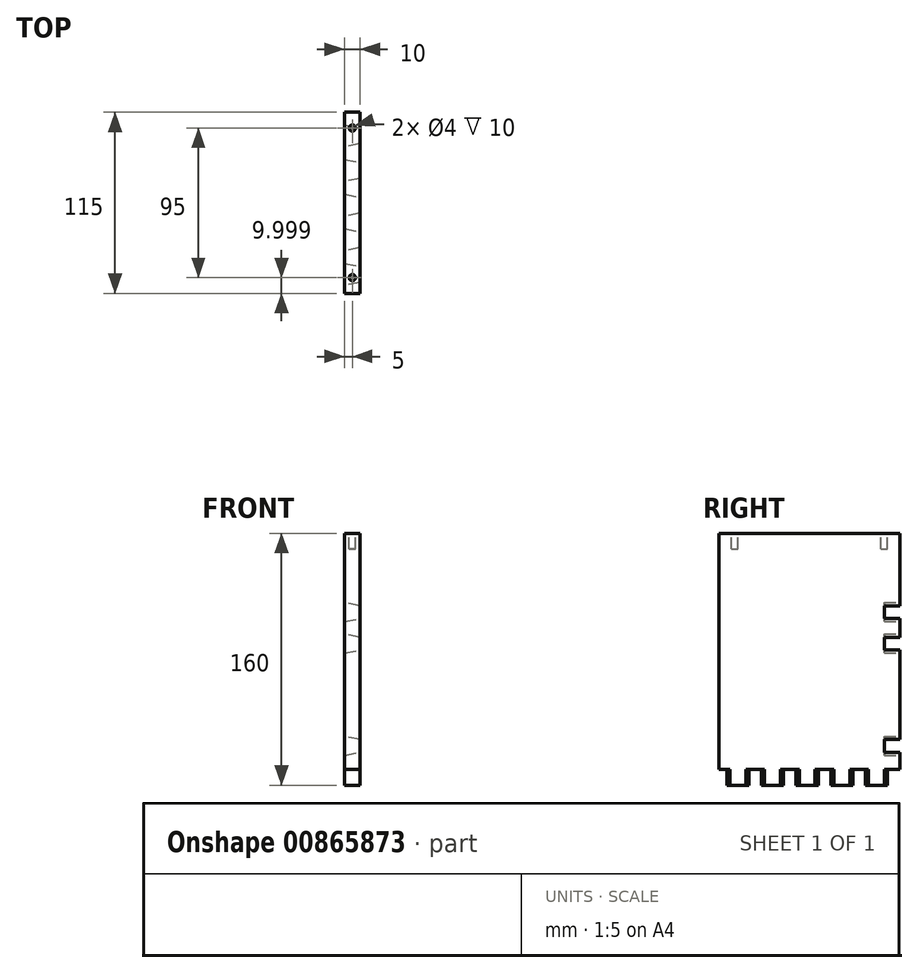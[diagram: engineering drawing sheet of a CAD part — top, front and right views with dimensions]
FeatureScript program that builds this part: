
annotation { "Feature Type Name" : "Feature", "Feature Type Description" : "" }
export const myFeature = defineFeature(function(context is Context, id is Id, definition is map)
    precondition{}
    {
        {
            var Q0;
            Q0=qCreatedBy(makeId("Right.planeOp"),FACE);
            var sketch = newSketch(context, id + "F0", { "sketchPlane" : qUnion([Q0])});
            skLineSegment(sketch, "E0.bottom", {"start": v(83.6, 91.6) * mm, "end": v(-31.4, 91.6) * mm});
            skLineSegment(sketch, "E0.left", {"start": v(83.6, 91.6) * mm, "end": v(83.6, -68.4) * mm});
            skLineSegment(sketch, "E0.right", {"start": v(-31.4, 91.6) * mm, "end": v(-31.4, -68.4) * mm});
            skLineSegment(sketch, "E1", {"start": v(83.6, -68.4) * mm, "end": v(-31.4, -68.4) * mm});
            skSolve(sketch);
        }
        {
            var Q0;
            Q0 = qSketchRegion(id + "F0", true);
            extrude(context, id + "F1", {"entities" : qUnion([Q0]), "depth" : 10 * mm, "offsetDistance" : 25 * mm});
        }
        {
            var Q0;
            Q0=makeQuery(id+"F1.opExtrude","SWEPT_FACE",FACE,{"disambiguationData":[OSD([sQuery(id+"F0.wireOp",EDGE,"E0.left")])]});
            var sketch = newSketch(context, id + "F2", { "sketchPlane" : qUnion([Q0])});
            skLineSegment(sketch, "E2", {"start": v(-10, 25.6) * mm, "end": v(0, 27.6) * mm});
            skLineSegment(sketch, "E3", {"start": v(0, 27.6) * mm, "end": v(0, 15.6) * mm});
            skLineSegment(sketch, "E4", {"start": v(0, 15.6) * mm, "end": v(-10, 17.6) * mm});
            skLineSegment(sketch, "E5", {"start": v(-10, 17.6) * mm, "end": v(-10, 25.6) * mm});
            skLineSegment(sketch, "E6", {"start": v(-10, 45.6) * mm, "end": v(0, 47.6) * mm});
            skLineSegment(sketch, "E7", {"start": v(0, 47.6) * mm, "end": v(0, 35.6) * mm});
            skLineSegment(sketch, "E8", {"start": v(0, 35.6) * mm, "end": v(-10, 37.6) * mm});
            skLineSegment(sketch, "E9", {"start": v(-10, 37.6) * mm, "end": v(-10, 45.6) * mm});
            skLineSegment(sketch, "E10", {"start": v(-10, -39.4) * mm, "end": v(0, -37.4) * mm});
            skLineSegment(sketch, "E11", {"start": v(0, -37.4) * mm, "end": v(0, -49.4) * mm});
            skLineSegment(sketch, "E12", {"start": v(0, -49.4) * mm, "end": v(-10, -47.4) * mm});
            skLineSegment(sketch, "E13", {"start": v(-10, -47.4) * mm, "end": v(-10, -39.4) * mm});
            skPoint(sketch, "E14", {"position": v(-10, 11.6) * mm});
            skSolve(sketch);
        }
        {
            var Q0;
            Q0 = qSketchRegion(id + "F2", true);
            extrude(context, id + "F3", {"entities" : qUnion([Q0]), "operationType" : NewBodyOperationType.REMOVE, "oppositeDirection" : true, "depth" : 10 * mm, "offsetDistance" : 25 * mm});
        }
        {
            var Q0;
            Q0=makeQuery(id+"F1.opExtrude","SWEPT_FACE",FACE,{"disambiguationData":[OSD([sQuery(id+"F0.wireOp",EDGE,"E1")])]});
            var sketch = newSketch(context, id + "F4", { "sketchPlane" : qUnion([Q0])});
            skLineSegment(sketch, "E15", {"start": v(10, -85.6) * mm, "end": v(0, -83.6) * mm});
            skLineSegment(sketch, "E16", {"start": v(0, -83.6) * mm, "end": v(0, -75.6) * mm});
            skLineSegment(sketch, "E17", {"start": v(0, -75.6) * mm, "end": v(10, -73.6) * mm});
            skLineSegment(sketch, "E18", {"start": v(10, -73.6) * mm, "end": v(10, -85.6) * mm});
            skLineSegment(sketch, "E19.0.1.0", {"start": v(0, -53.6) * mm, "end": v(10, -51.6) * mm});
            skLineSegment(sketch, "E19.0.1.1", {"start": v(10, -63.6) * mm, "end": v(0, -61.6) * mm});
            skLineSegment(sketch, "E19.0.1.2", {"start": v(10, -51.6) * mm, "end": v(10, -63.6) * mm});
            skLineSegment(sketch, "E19.0.1.3", {"start": v(0, -61.6) * mm, "end": v(0, -53.6) * mm});
            skLineSegment(sketch, "E19.0.2.0", {"start": v(0, -31.6) * mm, "end": v(10, -29.6) * mm});
            skLineSegment(sketch, "E19.0.2.1", {"start": v(10, -41.6) * mm, "end": v(0, -39.6) * mm});
            skLineSegment(sketch, "E19.0.2.2", {"start": v(10, -29.6) * mm, "end": v(10, -41.6) * mm});
            skLineSegment(sketch, "E19.0.2.3", {"start": v(0, -39.6) * mm, "end": v(0, -31.6) * mm});
            skLineSegment(sketch, "E19.0.3.0", {"start": v(0, -9.6) * mm, "end": v(10, -7.6) * mm});
            skLineSegment(sketch, "E19.0.3.1", {"start": v(10, -19.6) * mm, "end": v(0, -17.6) * mm});
            skLineSegment(sketch, "E19.0.3.2", {"start": v(10, -7.6) * mm, "end": v(10, -19.6) * mm});
            skLineSegment(sketch, "E19.0.3.3", {"start": v(0, -17.6) * mm, "end": v(0, -9.6) * mm});
            skLineSegment(sketch, "E19.0.4.0", {"start": v(0, 12.4) * mm, "end": v(10, 14.4) * mm});
            skLineSegment(sketch, "E19.0.4.1", {"start": v(10, 2.4) * mm, "end": v(0, 4.4) * mm});
            skLineSegment(sketch, "E19.0.4.2", {"start": v(10, 14.4) * mm, "end": v(10, 2.4) * mm});
            skLineSegment(sketch, "E19.0.4.3", {"start": v(0, 4.4) * mm, "end": v(0, 12.4) * mm});
            skLineSegment(sketch, "E19.direction1", {"start": v(0, -83.6) * mm, "end": v(25, -83.6) * mm, "construction": true});
            skLineSegment(sketch, "E19.direction2", {"start": v(0, -83.6) * mm, "end": v(0, -61.6) * mm, "construction": true});
            skLineSegment(sketch, "E20.0.0.5", {"start": v(0, 34.4) * mm, "end": v(10, 36.4) * mm});
            skLineSegment(sketch, "E20.3.0.5", {"start": v(10, 24.4) * mm, "end": v(0, 26.4) * mm});
            skLineSegment(sketch, "E20.6.0.5", {"start": v(10, 36.4) * mm, "end": v(10, 24.4) * mm});
            skLineSegment(sketch, "E20.9.0.5", {"start": v(0, 26.4) * mm, "end": v(0, 34.4) * mm});
            skSolve(sketch);
        }
        {
            var Q0;
            Q0 = qSketchRegion(id + "F4", true);
            extrude(context, id + "F5", {"entities" : qUnion([Q0]), "operationType" : NewBodyOperationType.REMOVE, "oppositeDirection" : true, "depth" : 10 * mm, "offsetDistance" : 25 * mm});
        }
        {
            var Q0;
            Q0=makeQuery(id+"F1.opExtrude","SWEPT_FACE",FACE,{"disambiguationData":[OSD([sQuery(id+"F0.wireOp",EDGE,"E0.bottom")])]});
            var sketch = newSketch(context, id + "F6", { "sketchPlane" : qUnion([Q0])});
            skCircle(sketch, "E21", {"center": v(5, 73.6) * mm, "radius": 2 * mm});
            skPoint(sketch, "E21.centerSnap0", {"position": v(5, 83.6) * mm});
            skCircle(sketch, "E22", {"center": v(5, -21.4) * mm, "radius": 2 * mm});
            skPoint(sketch, "E22.centerSnap0", {"position": v(5, -31.4) * mm});
            skSolve(sketch);
        }
        {
            var Q0;
            Q0 = qSketchRegion(id + "F6", true);
            extrude(context, id + "F7", {"entities" : qUnion([Q0]), "operationType" : NewBodyOperationType.REMOVE, "oppositeDirection" : true, "depth" : 10 * mm, "offsetDistance" : 25 * mm});
        }
    });
